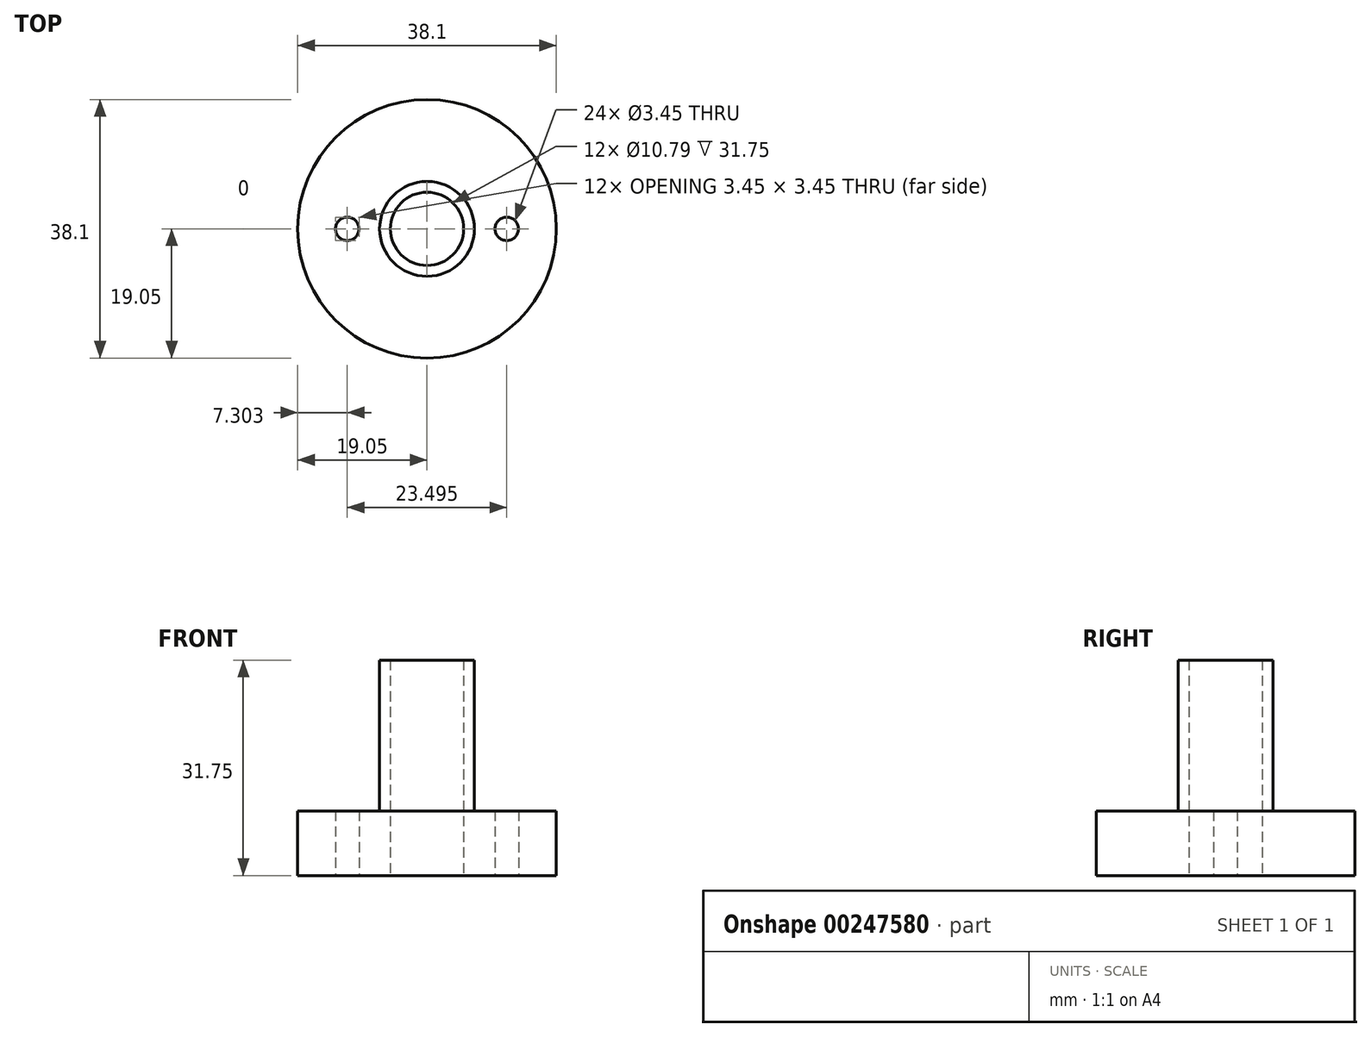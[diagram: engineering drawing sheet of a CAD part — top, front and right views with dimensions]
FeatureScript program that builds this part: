
annotation { "Feature Type Name" : "Feature", "Feature Type Description" : "" }
export const myFeature = defineFeature(function(context is Context, id is Id, definition is map)
    precondition{}
    {
        {
            var Q0;
            Q0=qCreatedBy(makeId("Right.planeOp"),FACE);
            var sketch = newSketch(context, id + "F0", { "sketchPlane" : qUnion([Q0])});
            skLineSegment(sketch, "E0", {"start": v(5.4, 31.75) * mm, "end": v(5.4, 0) * mm});
            skLineSegment(sketch, "E1", {"start": v(5.4, 0) * mm, "end": v(19.05, 0) * mm});
            skLineSegment(sketch, "E2", {"start": v(19.05, 0) * mm, "end": v(19.05, 9.53) * mm});
            skLineSegment(sketch, "E3", {"start": v(19.05, 9.53) * mm, "end": v(6.98, 9.53) * mm});
            skLineSegment(sketch, "E4", {"start": v(6.98, 9.53) * mm, "end": v(6.98, 31.75) * mm});
            skLineSegment(sketch, "E5", {"start": v(6.98, 31.75) * mm, "end": v(5.4, 31.75) * mm});
            skLineSegment(sketch, "E6", {"start": v(0, 0) * mm, "end": v(0, 32.35) * mm});
            skSolve(sketch);
        }
        {
            var Q0;
            Q0=makeQuery(id+"F0.imprint","IMPRINT",FACE,{"disambiguationData":[TD([[makeQuery(id+"F0.imprint","IMPRINT",EDGE,{"derivedFrom":sQuery(id+"F0.wireOp",EDGE,"E0")}),1.0]])]});
            var Q1;
            Q1 = qConstructionFilter(qBodyType(qCreatedBy(id + "F0" ,EDGE), BodyType.WIRE), ConstructionObject.NO);
            var Q2;
            Q2=sQuery(id+"F0.wireOp",EDGE,"E6");
            revolve(context, id + "F1", {"entities" : qUnion([Q0]), "surfaceEntities" : qUnion([Q1]), "axis" : qUnion([Q2]), "revolveType" : RevolveType.FULL});
        }
        {
            var Q0;
            Q0=makeQuery(id+"F1.opRevolve","SWEPT_FACE",FACE,{"disambiguationData":[OSD([sQuery(id+"F0.wireOp",EDGE,"E1")])]});
            var sketch = newSketch(context, id + "F2", { "sketchPlane" : qUnion([Q0])});
            skCircle(sketch, "E7", {"center": v(0, 0) * mm, "radius": 6.35 * mm, "construction": true});
            skPoint(sketch, "E8", {"position": v(-11.75, 0) * mm});
            skPoint(sketch, "E9", {"position": v(11.75, 0) * mm});
            skCircle(sketch, "E10", {"center": v(-11.75, 0) * mm, "radius": 6.35 * mm, "construction": true});
            skCircle(sketch, "E11", {"center": v(0, 0) * mm, "radius": 3.18 * mm, "construction": true});
            skLineSegment(sketch, "E12", {"start": v(-11.75, 0) * mm, "end": v(0, 0) * mm});
            skLineSegment(sketch, "E13", {"start": v(11.75, 0) * mm, "end": v(0, 0) * mm});
            skSolve(sketch);
        }
        {
            var Q0;
            Q0=sQuery(id+"F2.wireOp",VERTEX,"E8");
            var Q1;
            Q1=sQuery(id+"F2.wireOp",VERTEX,"E9");
            var Q2;
            Q2=makeQuery(id+"F1.opRevolve","SWEPT_BODY",BODY,{"disambiguationData":[OSD([sQuery(id+"F0.wireOp",EDGE,"E0"),sQuery(id+"F0.wireOp",EDGE,"E1"),sQuery(id+"F0.wireOp",EDGE,"E2"),sQuery(id+"F0.wireOp",EDGE,"E3"),sQuery(id+"F0.wireOp",EDGE,"E4"),sQuery(id+"F0.wireOp",EDGE,"E5")])]});
            hole(context, id + "F3", {"style" : HoleStyle.SIMPLE, "endStyle" : HoleEndStyle.THROUGH, "standardTappedOrClearance" : lookupTablePath({ "standard" : "ANSI", "engagement" : "75%", "pitch" : "32 tpi", "size" : "#8", "type" : "Tapped" }), "standardBlindInLast" : lookupTablePath({ "standard" : "ANSI", "engagement" : "75%", "pitch" : "32 tpi", "size" : "#8", "type" : "Tapped" }), "holeDiameter" : 3.45 * mm, "showTappedDepth" : true, "tappedDepth" : 12.7 * mm, "tapClearance" : 3, "locations" : qUnion([Q0, Q1]), "scope" : qUnion([Q2]), "majorDiameter" : 4.17 * mm});
        }
    });
